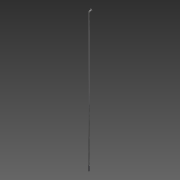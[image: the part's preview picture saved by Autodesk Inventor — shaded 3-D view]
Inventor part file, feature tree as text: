
AUTODESK INVENTOR PART (.ipt)
format: ipt  version: 2015 (Build 190159000, 159)  size: 115,712 bytes
history: native  units: mm
features: sketch x4, other x3, extrude x1, chamfer x1, thread x1
ambient origin geometry x8: Origin, YZ Plane, XZ Plane, XY Plane, X Axis, Y Axis, Z Axis, Center Point
bodies: Body1 (feature_tree)
feature tree (10):
  other  "Szprycha"
  other  "Bryła1"
  other  "Główka"
  extrude  "Połączenie z nyplem"  Depth=2.0mm
  chamfer  "Faza1"  Distance=266.0mm
  thread  "Gwint2"
  sketch  "Szkic1"
  sketch  "Szkic4"
  sketch  "Szkic5"
  sketch  "Szkic6"
